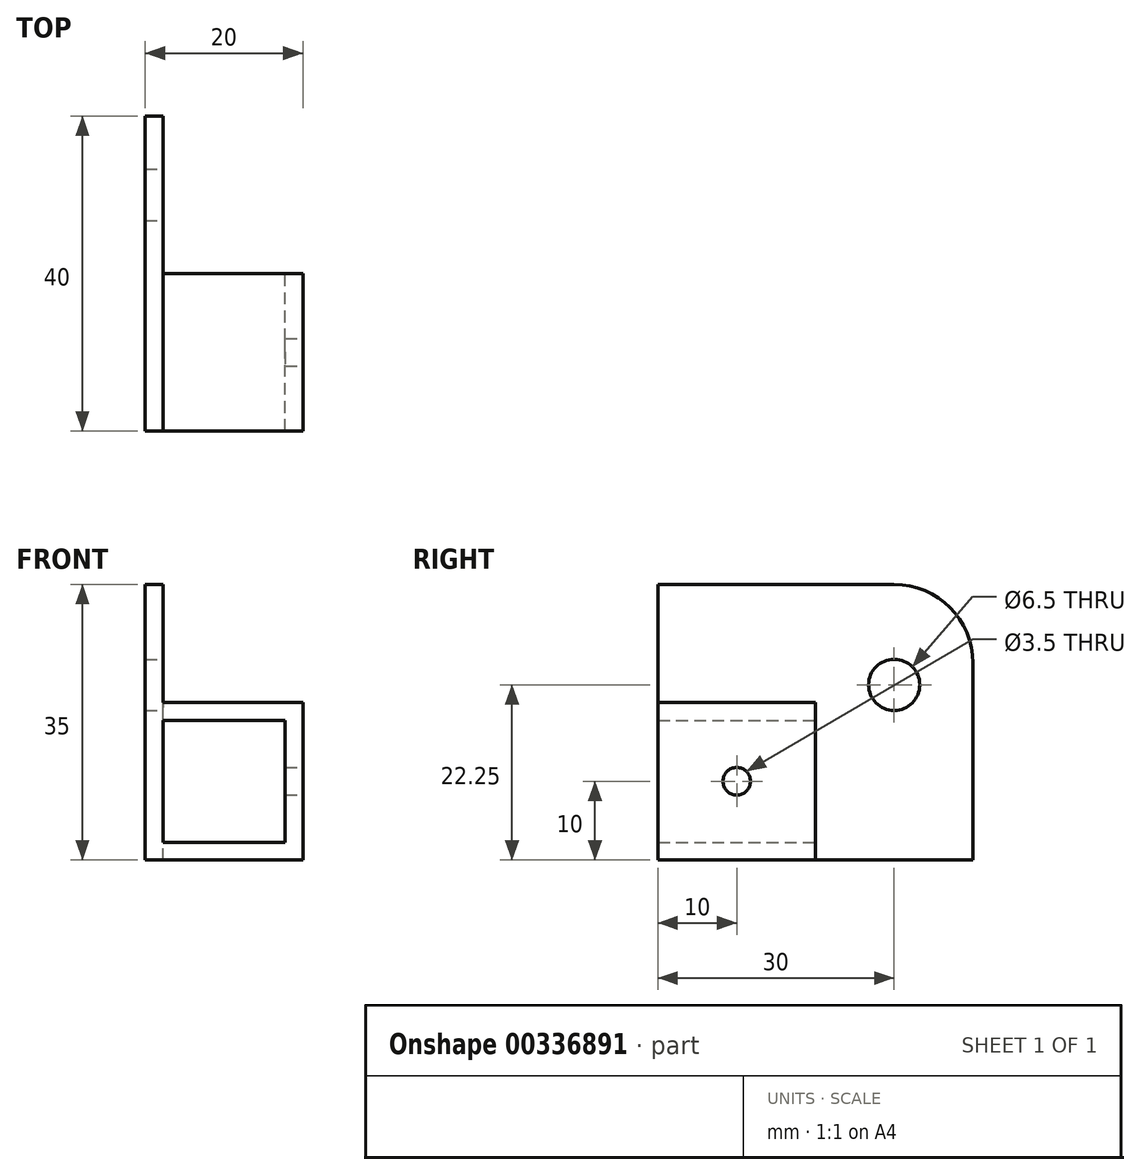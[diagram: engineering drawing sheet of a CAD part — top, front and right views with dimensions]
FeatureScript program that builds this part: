
annotation { "Feature Type Name" : "Feature", "Feature Type Description" : "" }
export const myFeature = defineFeature(function(context is Context, id is Id, definition is map)
    precondition{}
    {
        {
            var Q0;
            Q0=qCreatedBy(makeId("Top.planeOp"),FACE);
            var sketch = newSketch(context, id + "F0", { "sketchPlane" : qUnion([Q0])});
            skLineSegment(sketch, "E0.bottom", {"start": v(0, 0) * mm, "end": v(20, 0) * mm});
            skLineSegment(sketch, "E0.top", {"start": v(0, 20) * mm, "end": v(20, 20) * mm});
            skLineSegment(sketch, "E0.left", {"start": v(0, 0) * mm, "end": v(0, 20) * mm});
            skLineSegment(sketch, "E0.right", {"start": v(20, 0) * mm, "end": v(20, 20) * mm});
            skSolve(sketch);
        }
        {
            var Q0;
            Q0 = qSketchRegion(id + "F0", true);
            extrude(context, id + "F1", {"entities" : qUnion([Q0]), "depth" : 20 * mm});
        }
        {
            var Q0;
            Q0=makeQuery(id+"F1.opExtrude","SWEPT_FACE",FACE,{"disambiguationData":[OSD([sQuery(id+"F0.wireOp",EDGE,"E0.bottom")])]});
            var sketch = newSketch(context, id + "F2", { "sketchPlane" : qUnion([Q0])});
            skLineSegment(sketch, "E1.bottom", {"start": v(17.75, 2.25) * mm, "end": v(2.25, 2.25) * mm});
            skLineSegment(sketch, "E1.top", {"start": v(17.75, 17.75) * mm, "end": v(2.25, 17.75) * mm});
            skLineSegment(sketch, "E1.left", {"start": v(17.75, 2.25) * mm, "end": v(17.75, 17.75) * mm});
            skLineSegment(sketch, "E1.right", {"start": v(2.25, 2.25) * mm, "end": v(2.25, 17.75) * mm});
            skPoint(sketch, "E1.middle", {"position": v(10, 10) * mm});
            skPoint(sketch, "E1.middle.positionSnap0", {"position": v(0, 10) * mm});
            skPoint(sketch, "E1.middle.positionSnap1", {"position": v(10, 20) * mm});
            skPoint(sketch, "E1.centerSnap0", {"position": v(0, 10) * mm});
            skPoint(sketch, "E1.centerSnap1", {"position": v(10, 20) * mm});
            skSolve(sketch);
        }
        {
            var Q0;
            Q0=makeQuery(id+"F2.imprint","IMPRINT",FACE,{"disambiguationData":[TD([[makeQuery(id+"F2.imprint","IMPRINT",EDGE,{"derivedFrom":sQuery(id+"F2.wireOp",EDGE,"E1.bottom")}),-1.0]])]});
            extrude(context, id + "F3", {"entities" : qUnion([Q0]), "operationType" : NewBodyOperationType.REMOVE, "depth" : 25 * mm, "hasSecondDirection" : true, "secondDirectionOppositeDirection" : true, "secondDirectionDepth" : 25 * mm});
        }
        {
            var Q0;
            Q0=makeQuery(id+"F1.opExtrude","CAP_FACE",FACE,{"disambiguationData":[OSD([sQuery(id+"F0.wireOp",EDGE,"E0.bottom"),sQuery(id+"F0.wireOp",EDGE,"E0.top"),sQuery(id+"F0.wireOp",EDGE,"E0.left"),sQuery(id+"F0.wireOp",EDGE,"E0.right")])],"isStart":false});
            var sketch = newSketch(context, id + "F4", { "sketchPlane" : qUnion([Q0])});
            skLineSegment(sketch, "E2.bottom", {"start": v(0, 20) * mm, "end": v(2.25, 20) * mm});
            skLineSegment(sketch, "E2.top", {"start": v(0, 0) * mm, "end": v(2.25, 0) * mm});
            skLineSegment(sketch, "E2.left", {"start": v(0, 20) * mm, "end": v(0, 0) * mm});
            skLineSegment(sketch, "E2.right", {"start": v(2.25, 20) * mm, "end": v(2.25, 0) * mm});
            skSolve(sketch);
        }
        {
            var Q0;
            Q0=makeQuery(id+"F4.imprint","IMPRINT",FACE,{"disambiguationData":[TD([[makeQuery(id+"F4.imprint","IMPRINT",EDGE,{"derivedFrom":sQuery(id+"F4.wireOp",EDGE,"E2.bottom")}),-1.0]])]});
            extrude(context, id + "F5", {"entities" : qUnion([Q0]), "operationType" : NewBodyOperationType.ADD, "depth" : 15 * mm});
        }
        {
            var Q0;
            Q0=makeQuery(id+"F5.boolean.opBoolean","MERGE",FACE,{"derivedFrom":[makeQuery(id+"F1.opExtrude","SWEPT_FACE",FACE,{"disambiguationData":[OSD([sQuery(id+"F0.wireOp",EDGE,"E0.top")])]}),makeQuery(id+"F5.opExtrude","SWEPT_FACE",FACE,{"disambiguationData":[OSD([sQuery(id+"F4.wireOp",EDGE,"E2.bottom")])]})]});
            var sketch = newSketch(context, id + "F6", { "sketchPlane" : qUnion([Q0])});
            skLineSegment(sketch, "E3.bottom", {"start": v(0, 35) * mm, "end": v(-2.25, 35) * mm});
            skLineSegment(sketch, "E3.top", {"start": v(0, 0) * mm, "end": v(-2.25, 0) * mm});
            skLineSegment(sketch, "E3.left", {"start": v(0, 35) * mm, "end": v(0, 0) * mm});
            skLineSegment(sketch, "E3.right", {"start": v(-2.25, 35) * mm, "end": v(-2.25, 0) * mm});
            skSolve(sketch);
        }
        {
            var Q0;
            {var subQ6=sQuery(id+"F6.wireOp",EDGE,"E3.bottom");Q0=makeQuery(id+"F6.imprint","IMPRINT",FACE,{"disambiguationData":[TD([[makeQuery(id+"F6.imprint","IMPRINT",EDGE,{"derivedFrom":subQ6}),1.0]])]});}
            extrude(context, id + "F7", {"entities" : qUnion([Q0]), "operationType" : NewBodyOperationType.ADD, "depth" : 20 * mm});
        }
        {
            var Q0;
            Q0=makeQuery(id+"F7.boolean.opBoolean","MERGE",FACE,{"derivedFrom":[makeQuery(id+"F3.boolean.opBoolean","COPY",FACE,{"derivedFrom":makeQuery(id+"F3.opExtrude","SWEPT_FACE",FACE,{"disambiguationData":[OSD([sQuery(id+"F2.wireOp",EDGE,"E1.right")])]})}),makeQuery(id+"F5.opExtrude","SWEPT_FACE",FACE,{"disambiguationData":[OSD([sQuery(id+"F4.wireOp",EDGE,"E2.right")])]}),makeQuery(id+"F7.opExtrude","SWEPT_FACE",FACE,{"disambiguationData":[OSD([sQuery(id+"F6.wireOp",EDGE,"E3.right")])]})]});
            var sketch = newSketch(context, id + "F8", { "sketchPlane" : qUnion([Q0])});
            skCircle(sketch, "E4", {"center": v(30, 22.25) * mm, "radius": 3.25 * mm});
            skPoint(sketch, "E4.centerSnap0", {"position": v(30, 0) * mm});
            skSolve(sketch);
        }
        {
            var Q0;
            Q0=makeQuery(id+"F8.imprint","IMPRINT",FACE,{"disambiguationData":[TD([[makeQuery(id+"F8.imprint","IMPRINT",EDGE,{"derivedFrom":sQuery(id+"F8.wireOp",EDGE,"E4")}),1.0]])]});
            var Q1;
            Q1=sQuery(id+"F8.wireOp",EDGE,"E4");
            extrude(context, id + "F9", {"entities" : qUnion([Q0]), "operationType" : NewBodyOperationType.REMOVE, "surfaceEntities" : qUnion([Q1]), "oppositeDirection" : true, "depth" : 25 * mm, "hasSecondDirection" : true, "secondDirectionOppositeDirection" : false, "secondDirectionDepth" : 25 * mm});
        }
        {
            var Q0;
            Q0=makeQuery(id+"F1.opExtrude","SWEPT_FACE",FACE,{"disambiguationData":[OSD([sQuery(id+"F0.wireOp",EDGE,"E0.right")])]});
            var sketch = newSketch(context, id + "F10", { "sketchPlane" : qUnion([Q0])});
            skCircle(sketch, "E5", {"center": v(10, 10) * mm, "radius": 1.75 * mm});
            skPoint(sketch, "E5.centerSnap0", {"position": v(10, 20) * mm});
            skPoint(sketch, "E5.centerSnap1", {"position": v(20, 10) * mm});
            skSolve(sketch);
        }
        {
            var Q0;
            Q0=makeQuery(id+"F10.imprint","IMPRINT",FACE,{"disambiguationData":[TD([[makeQuery(id+"F10.imprint","IMPRINT",EDGE,{"derivedFrom":sQuery(id+"F10.wireOp",EDGE,"E5")}),1.0]])]});
            extrude(context, id + "F11", {"entities" : qUnion([Q0]), "operationType" : NewBodyOperationType.REMOVE, "oppositeDirection" : true, "depth" : 5 * mm});
        }
        {
            var Q0;
            Q0=makeQuery(id+"F7.opExtrude","CAP_EDGE",EDGE,{"disambiguationData":[OSD([sQuery(id+"F6.wireOp",EDGE,"E3.bottom")])],"isStart":false});
            fillet(context, id + "F12", {"entities" : qUnion([Q0]), "radius" : 10 * mm, "tangentPropagation" : true, "allowEdgeOverflow" : false});
        }
    });
